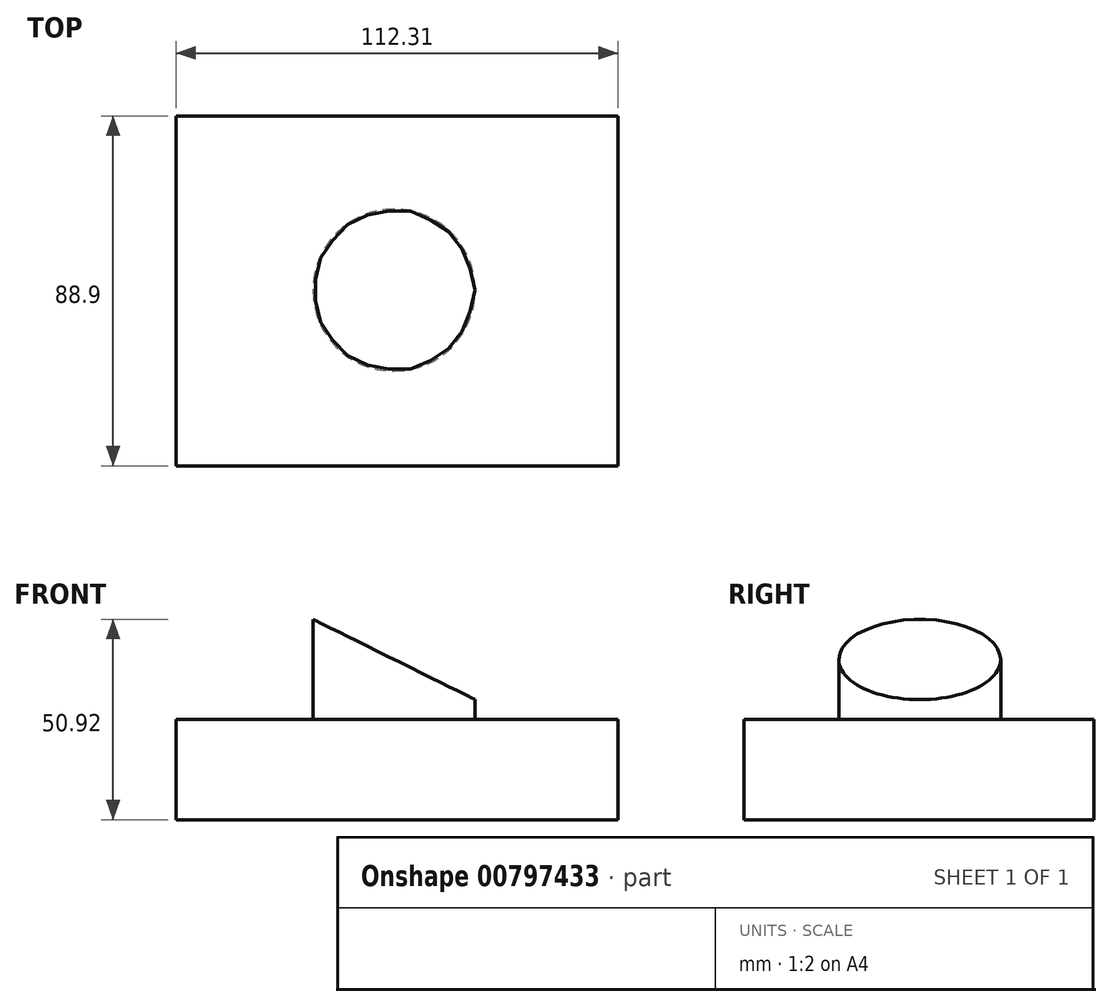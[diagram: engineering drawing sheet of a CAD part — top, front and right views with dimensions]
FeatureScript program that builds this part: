
annotation { "Feature Type Name" : "Feature", "Feature Type Description" : "" }
export const myFeature = defineFeature(function(context is Context, id is Id, definition is map)
    precondition{}
    {
        {
            var Q0;
            Q0=qCreatedBy(makeId("Front.planeOp"),FACE);
            var sketch = newSketch(context, id + "F0", { "sketchPlane" : qUnion([Q0])});
            skLineSegment(sketch, "E0.bottom", {"start": v(-74.45, 0) * mm, "end": v(37.86, 0) * mm});
            skLineSegment(sketch, "E0.top", {"start": v(-74.45, -25.53) * mm, "end": v(37.86, -25.53) * mm});
            skLineSegment(sketch, "E0.left", {"start": v(-74.45, 0) * mm, "end": v(-74.45, -25.53) * mm});
            skLineSegment(sketch, "E0.right", {"start": v(37.86, 0) * mm, "end": v(37.86, -25.53) * mm});
            skSolve(sketch);
        }
        {
            var Q0;
            Q0 = qSketchRegion(id + "F0", true);
            extrude(context, id + "F1", {"entities" : qUnion([Q0]), "oppositeDirection" : true, "depth" : 88.9 * mm, "offsetDistance" : 25.4 * mm});
        }
        {
            var Q0;
            Q0=qCreatedBy(makeId("Top.planeOp"),FACE);
            var sketch = newSketch(context, id + "F2", { "sketchPlane" : qUnion([Q0])});
            skCircle(sketch, "E1", {"center": v(-19.1, 44.6) * mm, "radius": 20.58 * mm});
            skSolve(sketch);
        }
        {
            var Q0;
            Q0 = qSketchRegion(id + "F2", true);
            extrude(context, id + "F3", {"entities" : qUnion([Q0]), "operationType" : NewBodyOperationType.ADD, "depth" : 25.4 * mm, "offsetDistance" : 25.4 * mm});
        }
        {
            var Q0;
            Q0=qCreatedBy(makeId("Front.planeOp"),FACE);
            var sketch = newSketch(context, id + "F4", { "sketchPlane" : qUnion([Q0])});
            skLineSegment(sketch, "E2", {"start": v(-63.46, 37.2) * mm, "end": v(5.16, 3.15) * mm});
            skLineSegment(sketch, "E3", {"start": v(5.16, 3.15) * mm, "end": v(5.16, 39.87) * mm});
            skLineSegment(sketch, "E4", {"start": v(5.16, 39.87) * mm, "end": v(-63.46, 37.2) * mm});
            skSolve(sketch);
        }
        {
            var Q0;
            Q0=makeQuery(id+"F4.imprint","IMPRINT",FACE,{"disambiguationData":[TD([[makeQuery(id+"F4.imprint","IMPRINT",EDGE,{"derivedFrom":sQuery(id+"F4.wireOp",EDGE,"E2")}),1.0]])]});
            extrude(context, id + "F5", {"entities" : qUnion([Q0]), "operationType" : NewBodyOperationType.REMOVE, "oppositeDirection" : true, "depth" : 177.8 * mm, "offsetDistance" : 25.4 * mm});
        }
    });
